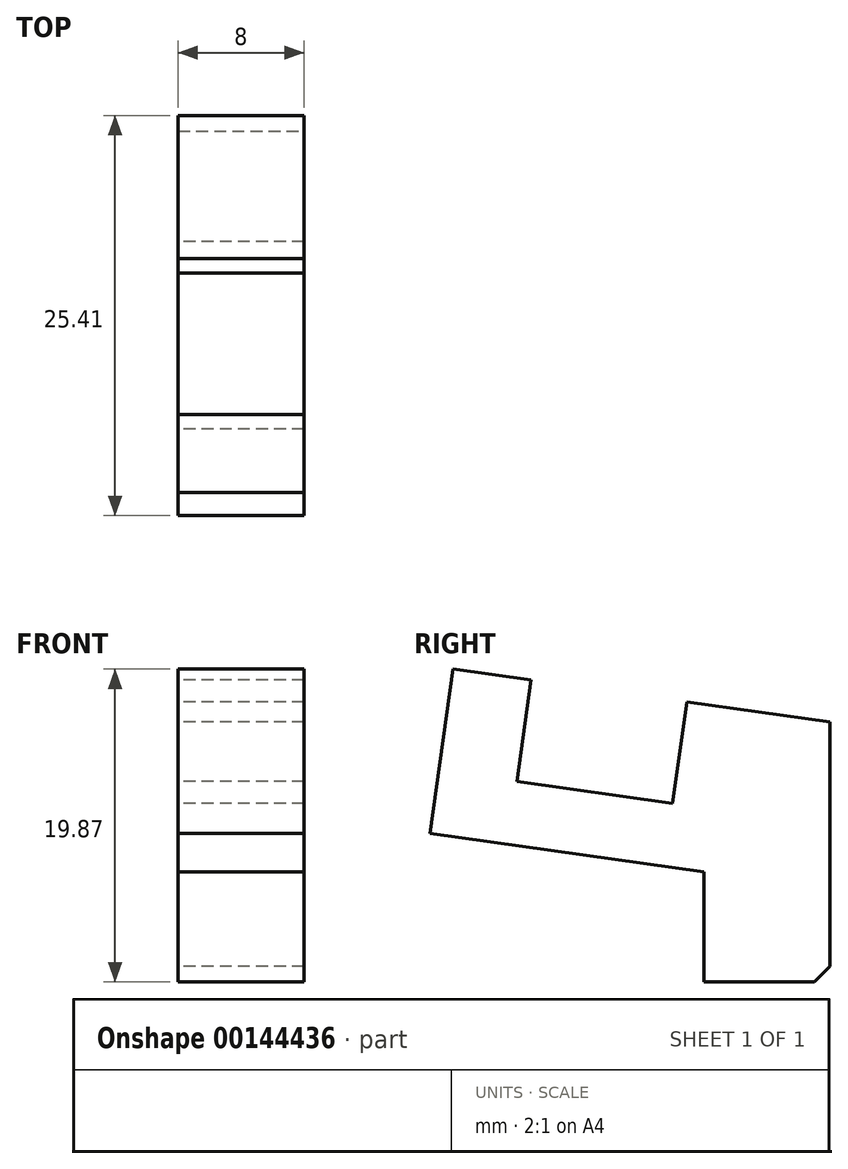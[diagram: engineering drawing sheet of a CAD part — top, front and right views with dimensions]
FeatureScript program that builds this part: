
annotation { "Feature Type Name" : "Feature", "Feature Type Description" : "" }
export const myFeature = defineFeature(function(context is Context, id is Id, definition is map)
    precondition{}
    {
        {
            var Q0;
            Q0=qCreatedBy(makeId("Right.planeOp"),FACE);
            var sketch = newSketch(context, id + "F0", { "sketchPlane" : qUnion([Q0])});
            skLineSegment(sketch, "E0", {"start": v(0, 0) * mm, "end": v(0, -7) * mm});
            skLineSegment(sketch, "E1", {"start": v(0, -7) * mm, "end": v(8, -7) * mm});
            skLineSegment(sketch, "E2", {"start": v(8, -7) * mm, "end": v(8, 9.5) * mm});
            skLineSegment(sketch, "E3", {"start": v(-15.95, 12.87) * mm, "end": v(-17.41, 2.45) * mm});
            skLineSegment(sketch, "E4", {"start": v(-17.41, 2.45) * mm, "end": v(0, 0) * mm});
            skLineSegment(sketch, "E5", {"start": v(-15.95, 12.87) * mm, "end": v(-11, 12.17) * mm});
            skLineSegment(sketch, "E6", {"start": v(-11, 12.17) * mm, "end": v(-11.9, 5.73) * mm});
            skLineSegment(sketch, "E7", {"start": v(-11.9, 5.73) * mm, "end": v(-2, 4.34) * mm});
            skLineSegment(sketch, "E8", {"start": v(-2, 4.34) * mm, "end": v(-1.1, 10.78) * mm});
            skLineSegment(sketch, "E9", {"start": v(-1.1, 10.78) * mm, "end": v(8, 9.5) * mm});
            skSolve(sketch);
        }
        {
            var Q0;
            Q0 = qSketchRegion(id + "F0", true);
            extrude(context, id + "F1", {"entities" : qUnion([Q0]), "depth" : 8 * mm});
        }
        {
            var Q0;
            Q0=makeQuery(id+"F1.opExtrude","SWEPT_EDGE",EDGE,{"disambiguationData":[OSD([sQuery(id+"F0.wireOp",EDGE,"E1"),sQuery(id+"F0.wireOp",EDGE,"E2")])]});
            chamfer(context, id + "F2", {"entities" : qUnion([Q0]), "width" : 1 * mm, "tangentPropagation" : true});
        }
    });
